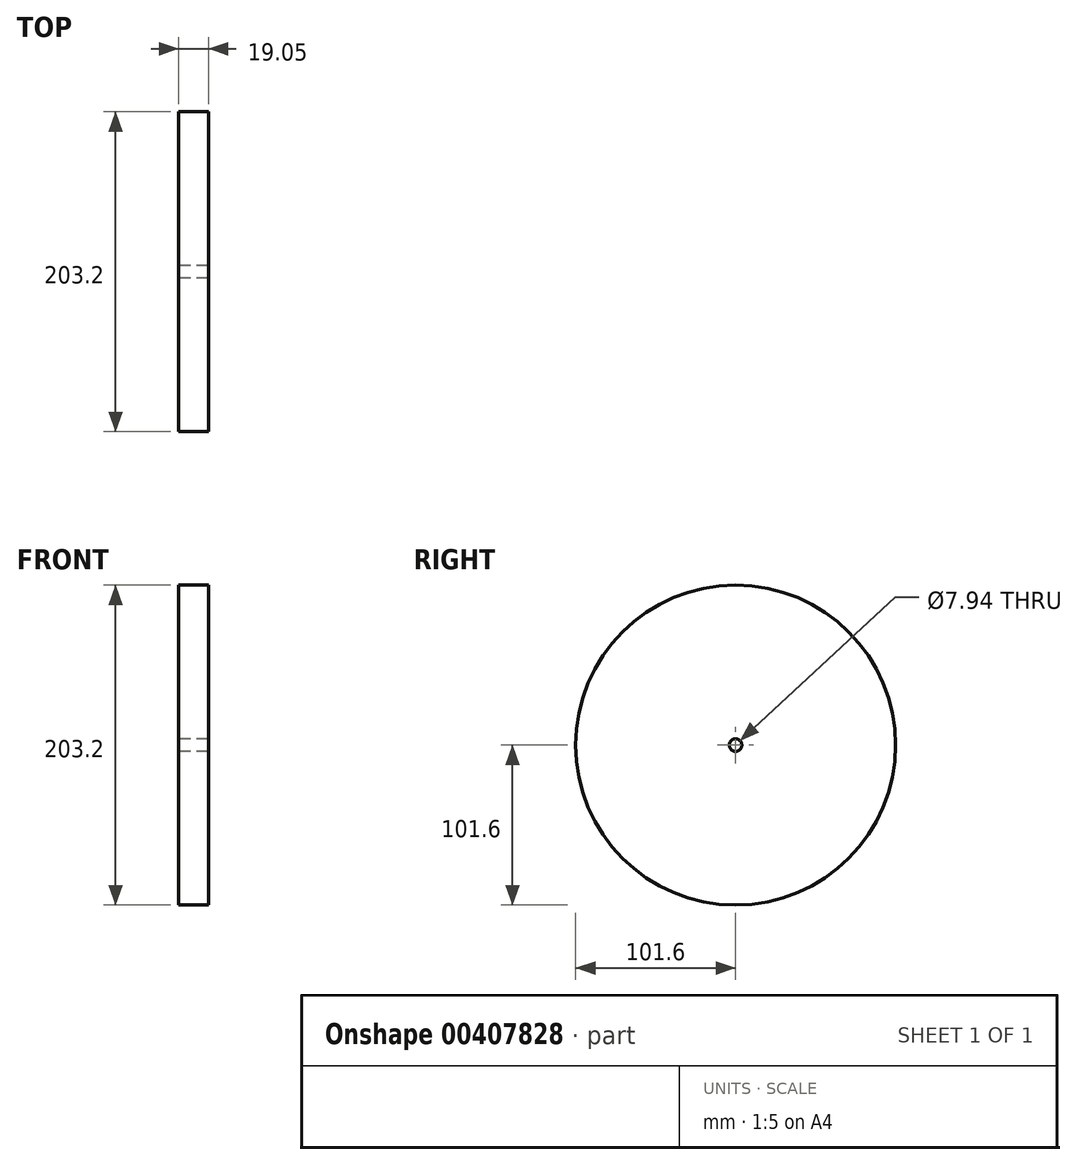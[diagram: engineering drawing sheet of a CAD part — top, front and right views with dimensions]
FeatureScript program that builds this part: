
annotation { "Feature Type Name" : "Feature", "Feature Type Description" : "" }
export const myFeature = defineFeature(function(context is Context, id is Id, definition is map)
    precondition{}
    {
        {
            var Q0;
            Q0=qCreatedBy(makeId("Right.planeOp"),FACE);
            var sketch = newSketch(context, id + "F0", { "sketchPlane" : qUnion([Q0])});
            skCircle(sketch, "E0", {"center": v(0, 0) * mm, "radius": 101.6 * mm});
            skCircle(sketch, "E1", {"center": v(0, 0) * mm, "radius": 3.97 * mm});
            skSolve(sketch);
        }
        {
            var Q0;
            Q0=makeQuery(id+"F0.imprint","IMPRINT",FACE,{"disambiguationData":[TD([[makeQuery(id+"F0.imprint","IMPRINT",EDGE,{"derivedFrom":sQuery(id+"F0.wireOp",EDGE,"E0")}),1.0]])]});
            extrude(context, id + "F1", {"entities" : qUnion([Q0]), "depth" : 19.05 * mm});
        }
    });
